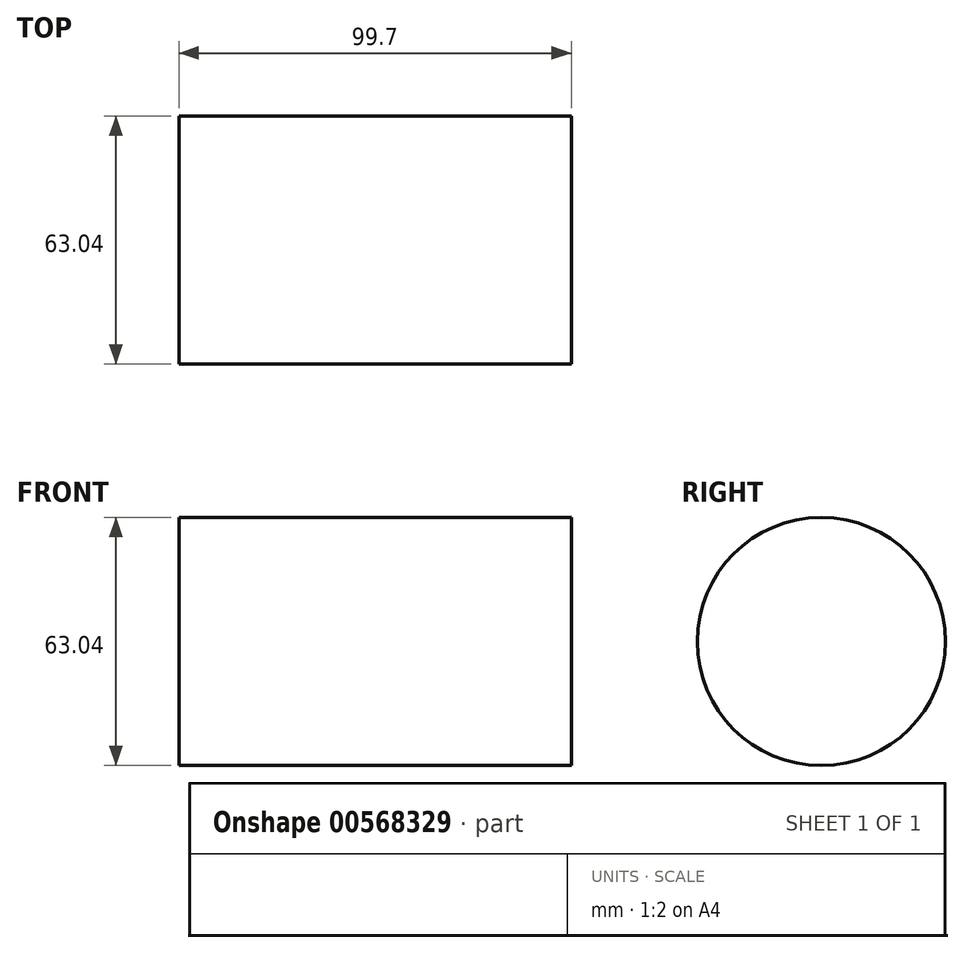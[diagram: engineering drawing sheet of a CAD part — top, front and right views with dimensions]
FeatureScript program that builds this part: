
annotation { "Feature Type Name" : "Feature", "Feature Type Description" : "" }
export const myFeature = defineFeature(function(context is Context, id is Id, definition is map)
    precondition{}
    {
        {
            var Q0;
            Q0=qCreatedBy(makeId("Right.planeOp"),FACE);
            var sketch = newSketch(context, id + "F0", { "sketchPlane" : qUnion([Q0])});
            skCircle(sketch, "E0", {"center": v(0, 0) * mm, "radius": 31.52 * mm});
            skSolve(sketch);
        }
        {
            var Q0;
            Q0=sQuery(id+"F0.wireOp",EDGE,"E0");
            extrude(context, id + "F1", {"bodyType" : ToolBodyType.SURFACE, "surfaceEntities" : qUnion([Q0]), "endBound" : BoundingType.SYMMETRIC, "depth" : 99.7 * mm, "offsetDistance" : 25.4 * mm});
        }
    });
